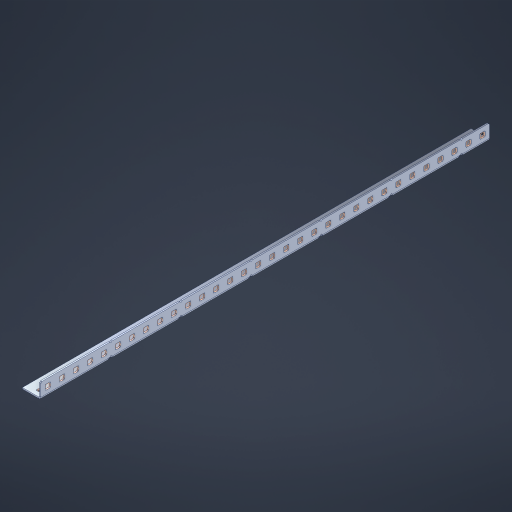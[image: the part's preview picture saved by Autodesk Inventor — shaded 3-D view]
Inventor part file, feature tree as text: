
AUTODESK INVENTOR PART (.ipt)
format: ipt  version: 2023 (Build 270158000, 158)  size: 991,232 bytes
history: native  units: in
note: dims shown in document units (in); Inventor stores cm internally (conversion verified against a paired STEP export)
features: other x69, extrude x63, sheet_metal_op x10, sketch x8, mirror x1, pattern_linear x1, chamfer x1
ambient origin geometry x8: Origin, YZ Plane, XZ Plane, XY Plane, X Axis, Y Axis, Z Axis, Center Point
bodies: Solid1 (feature_tree), Body (feature_tree)
feature tree (153):
  other  "Flange Pattern Plane"
  sheet_metal_op  "Flange Pattern"
  sheet_metal_op  "Body Pattern"
  other  "Arc Length"
  mirror  "Notch Mirror"
  pattern_linear  "Notch Pattern"  Spacing1=0.1875in  [1 undecoded]
  chamfer  "End Chamfer"
  extrude  "Half Cut"  Depth=0.0469in
  sketch  "Sketch1"  dims[d0=2.5in]
  other  "Plate1"
  sketch  "Sketch2"  dims[d1=16.0in]
  other  "Plate2"
  sheet_metal_op  "Bend1"
  sheet_metal_op  "Corner1"
  sketch  "Sketch3"  dims[d2=0.0469in]
  other  "Flange Pattern Sketch"
  sketch  "Sketch7"  dims[d3=0.0469in]
  other  "Srf1"
  other  "Srf2"
  sketch  "Sketch8"  dims[d4=0.0234in]
  sketch  "Sketch9"  dims[d5=0.0938in]
  other  "Srf91"
  sheet_metal_op  "Body Pattern Sketch"
  other  "Srf92"
  sketch  "Sketch13"  dims[d6=0.0469in]
  sketch  "Sketch14"  dims[d7=0.5in d8=90.0deg d9=0.0312in d10=0.1875in d11=0.0469in d12=0.0469in d16=0.182in d17=0.02in d18=0.0469in d19=0.0in d20=0.25in d21=0.25in d46=0.172in d47=1.0in d48=0.0in d49=0.182in d50=0.02in d51=0.25in d52=0.25in d53=0.0469in d54=0.0in d55=0.172in d56=1.0in d57=0.0in d60=12.5984in d62=0.5in d63=0.3937in d65=0.5in d85=0.1227in d86=0.1659in d88=0.04in d89=0.0469in d90=0.0in d91=0.04in d92=0.0491in d95=2.5in d96=0.04in d97=0.25in d98=45.0deg d101=0.0in d102=2.497in d131=0.5in d132=12.5984in d134=0.5in d139=0.5in]
  other  "Srf856"
  other  "Srf1310"
  other  "Srf1311"
  other  "Srf1312"
  other  "Srf1376"
  other  "Srf1377"
  other  "Srf1728"
  other  "Srf1755"
  other  "Srf1878"
  other  "Srf1879"
  other  "Srf1880"
  other  "Srf1881"
  other  "Srf1882"
  other  "Srf1883"
  other  "Srf1884"
  other  "Srf1885"
  other  "Srf1886"
  other  "Srf1887"
  other  "Srf1888"
  other  "Srf1889"
  other  "Srf1890"
  other  "Srf1891"
  other  "Srf1892"
  other  "Srf1893"
  other  "Srf1894"
  other  "Srf1895"
  other  "Srf1896"
  other  "Srf1897"
  other  "Srf1898"
  other  "Srf1899"
  other  "Srf1900"
  other  "Srf1901"
  other  "Srf1902"
  other  "Srf1903"
  other  "Srf1942"
  other  "Srf1943"
  other  "Srf1944"
  other  "Srf1945"
  other  "Srf1946"
  other  "Srf1947"
  other  "Srf1948"
  other  "Srf1949"
  other  "Srf1950"
  other  "Srf1951"
  other  "Srf1952"
  other  "Srf1953"
  other  "Srf1954"
  other  "Srf1955"
  other  "Srf1956"
  other  "Srf1957"
  other  "Srf1958"
  other  "Srf1959"
  other  "Srf1960"
  other  "Srf1961"
  other  "Srf1962"
  other  "Srf1963"
  other  "Srf1964"
  other  "Srf1965"
  other  "Srf1966"
  other  "Srf1967"
  sheet_metal_op  "Flange Stamp"
  sheet_metal_op  "Flange Circle"
  sheet_metal_op  "Body Stamp"
  sheet_metal_op  "Body Circle"
  sheet_metal_op  "Notch"
  extrude  "ExtrusionSrf2"  Depth=0.0469in
  extrude  "ExtrusionSrf92"  Depth=0.5in
  extrude  "ExtrusionSrf856"  Depth=0.02in
  extrude  "ExtrusionSrf1310"  Depth=0.0469in
  extrude  "ExtrusionSrf1311"  TaperAngle=0.0deg  [1 undecoded]
  extrude  "ExtrusionSrf1312"  Depth=0.5in
  extrude  "ExtrusionSrf1376"  Depth=0.5in
  extrude  "ExtrusionSrf1377"  Depth=0.5in
  extrude  "ExtrusionSrf1728"  Depth=0.5in TaperAngle=0.0deg
  extrude  "ExtrusionSrf1755"  Depth=0.5in
  extrude  "ExtrusionSrf1878"  Depth=0.02in
  extrude  "ExtrusionSrf1879"  Depth=0.5in
  extrude  "ExtrusionSrf1880"  Depth=0.5in
  extrude  "ExtrusionSrf1881"  Depth=0.0469in
  extrude  "ExtrusionSrf1882"  TaperAngle=0.0deg  [1 undecoded]
  extrude  "ExtrusionSrf1883"  Depth=0.5in
  extrude  "ExtrusionSrf1884"  Depth=0.5in TaperAngle=0.0deg
  extrude  "ExtrusionSrf1885"  Depth=0.5in
  extrude  "ExtrusionSrf1886"  Depth=0.5in
  extrude  "ExtrusionSrf1887"  Depth=0.5in
  extrude  "ExtrusionSrf1888"  Depth=0.5in
  extrude  "ExtrusionSrf1889"  Depth=0.5in
  extrude  "ExtrusionSrf1890"  Depth=0.0469in
  extrude  "ExtrusionSrf1891"  TaperAngle=0.0deg  [1 undecoded]
  extrude  "ExtrusionSrf1892"  Depth=0.5in
  extrude  "ExtrusionSrf1893"  Depth=0.5in
  extrude  "ExtrusionSrf1894"  Depth=0.5in
  extrude  "ExtrusionSrf1895"  Depth=0.5in TaperAngle=45.0deg
  extrude  "ExtrusionSrf1896"  TaperAngle=0.0deg  [1 undecoded]
  extrude  "ExtrusionSrf1897"  Depth=0.5in
  extrude  "ExtrusionSrf1898"  Depth=0.5in
  extrude  "ExtrusionSrf1899"  Depth=0.5in
  extrude  "ExtrusionSrf1900"  Depth=0.5in
  extrude  "ExtrusionSrf1901"  Depth=0.5in
  extrude  "ExtrusionSrf1902"  [1 undecoded]
  extrude  "ExtrusionSrf1903"  [1 undecoded]
  extrude  "ExtrusionSrf1942"  [1 undecoded]
  extrude  "ExtrusionSrf1943"  [1 undecoded]
  extrude  "ExtrusionSrf1944"  [1 undecoded]
  extrude  "ExtrusionSrf1945"  [1 undecoded]
  extrude  "ExtrusionSrf1946"  [1 undecoded]
  extrude  "ExtrusionSrf1947"  [1 undecoded]
  extrude  "ExtrusionSrf1948"  [1 undecoded]
  extrude  "ExtrusionSrf1949"  [1 undecoded]
  extrude  "ExtrusionSrf1950"  [1 undecoded]
  extrude  "ExtrusionSrf1951"  [1 undecoded]
  extrude  "ExtrusionSrf1952"  [1 undecoded]
  extrude  "ExtrusionSrf1953"  [1 undecoded]
  extrude  "ExtrusionSrf1954"  [1 undecoded]
  extrude  "ExtrusionSrf1955"  [1 undecoded]
  extrude  "ExtrusionSrf1956"  [1 undecoded]
  extrude  "ExtrusionSrf1957"  [1 undecoded]
  extrude  "ExtrusionSrf1958"  [1 undecoded]
  extrude  "ExtrusionSrf1959"  [1 undecoded]
  extrude  "ExtrusionSrf1960"  [1 undecoded]
  extrude  "ExtrusionSrf1961"  [1 undecoded]
  extrude  "ExtrusionSrf1962"  [1 undecoded]
  extrude  "ExtrusionSrf1963"  [1 undecoded]
  extrude  "ExtrusionSrf1964"  [1 undecoded]
  extrude  "ExtrusionSrf1965"  [1 undecoded]
  extrude  "ExtrusionSrf1966"  [1 undecoded]
  extrude  "ExtrusionSrf1967"  [1 undecoded]
note: 33 required parameter values undecoded (feature->parameter linkage not recoverable at this tier; creation-order binding heuristic only, values carry confidence <= 0.55)
